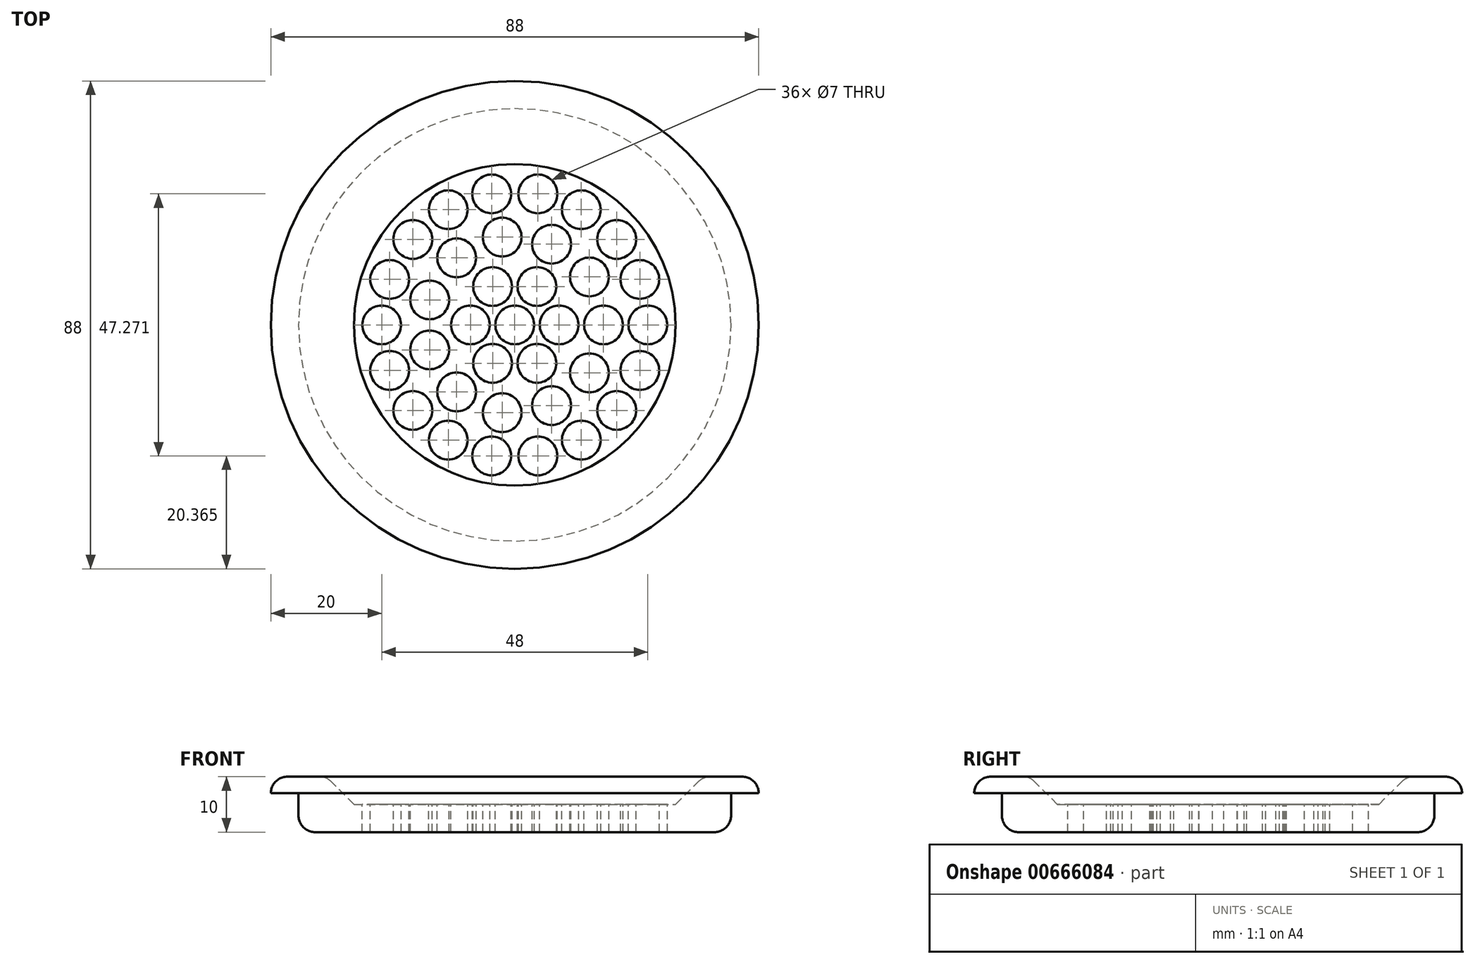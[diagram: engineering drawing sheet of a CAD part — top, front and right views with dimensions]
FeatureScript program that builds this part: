
annotation { "Feature Type Name" : "Feature", "Feature Type Description" : "" }
export const myFeature = defineFeature(function(context is Context, id is Id, definition is map)
    precondition{}
    {
        {
            var Q0;
            Q0=qCreatedBy(makeId("Front.planeOp"),FACE);
            var sketch = newSketch(context, id + "F0", { "sketchPlane" : qUnion([Q0])});
            skLineSegment(sketch, "E0", {"start": v(0, -3) * mm, "end": v(0, -3) * mm});
            skLineSegment(sketch, "E1", {"start": v(0, -3) * mm, "end": v(5, -3) * mm});
            skLineSegment(sketch, "E2", {"start": v(5, -3) * mm, "end": v(5, -7) * mm});
            skLineSegment(sketch, "E3", {"start": v(8, -10) * mm, "end": v(44, -10) * mm});
            skLineSegment(sketch, "E4", {"start": v(44, -10) * mm, "end": v(44, -5) * mm});
            skLineSegment(sketch, "E5", {"start": v(44, -5) * mm, "end": v(15, -5) * mm});
            skLineSegment(sketch, "E6", {"start": v(15, -5) * mm, "end": v(10.88, -0.88) * mm});
            skLineSegment(sketch, "E7", {"start": v(8.76, 0) * mm, "end": v(3, 0) * mm});
            skPoint(sketch, "E8.visualSharp", {"position": v(5, -10) * mm});
            skArc(sketch, "E8.filletArc", {"start": v(5, -7) * mm, "mid": v(5.88, -9.12) * mm, "end": v(8, -10) * mm});
            skPoint(sketch, "E9.visualSharp", {"position": v(0, 0) * mm});
            skArc(sketch, "E9.filletArc", {"start": v(3, 0) * mm, "mid": v(0.88, -0.88) * mm, "end": v(0, -3) * mm});
            skPoint(sketch, "E10.visualSharp", {"position": v(10, 0) * mm});
            skArc(sketch, "E10.filletArc", {"start": v(10.88, -0.88) * mm, "mid": v(9.9, -0.23) * mm, "end": v(8.76, 0) * mm});
            skLineSegment(sketch, "E11", {"start": v(44, -10) * mm, "end": v(44, 10.7) * mm, "construction": true});
            skSolve(sketch);
        }
        {
            var Q0;
            Q0=makeQuery(id+"F0.imprint","IMPRINT",FACE,{"disambiguationData":[TD([[makeQuery(id+"F0.imprint","IMPRINT",EDGE,{"derivedFrom":sQuery(id+"F0.wireOp",EDGE,"E1")}),1.0]])]});
            var Q1;
            Q1=sQuery(id+"F0.wireOp",EDGE,"E11");
            revolve(context, id + "F1", {"entities" : qUnion([Q0]), "axis" : qUnion([Q1]), "revolveType" : RevolveType.FULL});
        }
        {
            var Q0;
            Q0=makeQuery(id+"F1.opRevolve","SWEPT_FACE",FACE,{"disambiguationData":[OSD([sQuery(id+"F0.wireOp",EDGE,"E5")])]});
            var sketch = newSketch(context, id + "F2", { "sketchPlane" : qUnion([Q0])});
            skCircle(sketch, "E12", {"center": v(44, 0) * mm, "radius": 3.5 * mm});
            skCircle(sketch, "E13.1.0.0", {"center": v(52, 0) * mm, "radius": 3.5 * mm});
            skCircle(sketch, "E13.2.0.0", {"center": v(60, 0) * mm, "radius": 3.5 * mm});
            skCircle(sketch, "E13.3.0.0", {"center": v(68, 0) * mm, "radius": 3.5 * mm});
            skLineSegment(sketch, "E13.direction1", {"start": v(44, 0) * mm, "end": v(52, 0) * mm, "construction": true});
            skCircle(sketch, "E14.1.0", {"center": v(48, 6.93) * mm, "radius": 3.5 * mm});
            skCircle(sketch, "E14.2.0", {"center": v(40, 6.93) * mm, "radius": 3.5 * mm});
            skCircle(sketch, "E14.3.0", {"center": v(36, 0) * mm, "radius": 3.5 * mm});
            skCircle(sketch, "E14.4.0", {"center": v(40, -6.93) * mm, "radius": 3.5 * mm});
            skCircle(sketch, "E14.5.0", {"center": v(48, -6.93) * mm, "radius": 3.5 * mm});
            skCircle(sketch, "E15.1.0", {"center": v(57.46, 8.65) * mm, "radius": 3.5 * mm});
            skCircle(sketch, "E15.2.0", {"center": v(50.65, 14.55) * mm, "radius": 3.5 * mm});
            skCircle(sketch, "E15.3.0", {"center": v(41.72, 15.84) * mm, "radius": 3.5 * mm});
            skCircle(sketch, "E15.4.0", {"center": v(33.52, 12.1) * mm, "radius": 3.5 * mm});
            skCircle(sketch, "E15.5.0", {"center": v(28.65, 4.5) * mm, "radius": 3.5 * mm});
            skCircle(sketch, "E15.6.0", {"center": v(28.65, -4.5) * mm, "radius": 3.5 * mm});
            skCircle(sketch, "E15.7.0", {"center": v(33.52, -12.1) * mm, "radius": 3.5 * mm});
            skCircle(sketch, "E15.8.0", {"center": v(41.72, -15.84) * mm, "radius": 3.5 * mm});
            skCircle(sketch, "E15.9.0", {"center": v(50.65, -14.55) * mm, "radius": 3.5 * mm});
            skCircle(sketch, "E15.10.0", {"center": v(57.46, -8.65) * mm, "radius": 3.5 * mm});
            skCircle(sketch, "E16.1.0", {"center": v(66.55, 8.2) * mm, "radius": 3.5 * mm});
            skCircle(sketch, "E16.2.0", {"center": v(62.39, 15.43) * mm, "radius": 3.5 * mm});
            skCircle(sketch, "E16.3.0", {"center": v(56, 20.78) * mm, "radius": 3.5 * mm});
            skCircle(sketch, "E16.4.0", {"center": v(48.17, 23.64) * mm, "radius": 3.5 * mm});
            skCircle(sketch, "E16.5.0", {"center": v(39.83, 23.64) * mm, "radius": 3.5 * mm});
            skCircle(sketch, "E16.6.0", {"center": v(32, 20.78) * mm, "radius": 3.5 * mm});
            skCircle(sketch, "E16.7.0", {"center": v(25.61, 15.43) * mm, "radius": 3.5 * mm});
            skCircle(sketch, "E16.8.0", {"center": v(21.45, 8.2) * mm, "radius": 3.5 * mm});
            skCircle(sketch, "E16.9.0", {"center": v(20, 0) * mm, "radius": 3.5 * mm});
            skCircle(sketch, "E16.10.0", {"center": v(21.45, -8.2) * mm, "radius": 3.5 * mm});
            skCircle(sketch, "E16.11.0", {"center": v(25.61, -15.43) * mm, "radius": 3.5 * mm});
            skCircle(sketch, "E16.12.0", {"center": v(32, -20.78) * mm, "radius": 3.5 * mm});
            skCircle(sketch, "E16.13.0", {"center": v(39.83, -23.64) * mm, "radius": 3.5 * mm});
            skCircle(sketch, "E16.14.0", {"center": v(48.17, -23.64) * mm, "radius": 3.5 * mm});
            skCircle(sketch, "E16.15.0", {"center": v(56, -20.78) * mm, "radius": 3.5 * mm});
            skCircle(sketch, "E16.16.0", {"center": v(62.39, -15.43) * mm, "radius": 3.5 * mm});
            skCircle(sketch, "E16.17.0", {"center": v(66.55, -8.2) * mm, "radius": 3.5 * mm});
            skSolve(sketch);
        }
        {
            var Q0;
            Q0 = qSketchRegion(id + "F2", true);
            extrude(context, id + "F3", {"entities" : qUnion([Q0]), "operationType" : NewBodyOperationType.REMOVE, "endBound" : BoundingType.UP_TO_NEXT, "oppositeDirection" : true, "depth" : 25 * mm, "offsetDistance" : 25 * mm});
        }
    });
